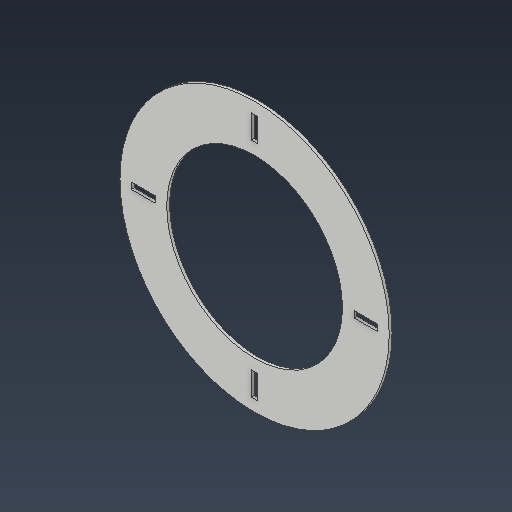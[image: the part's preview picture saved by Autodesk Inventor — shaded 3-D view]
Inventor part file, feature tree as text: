
AUTODESK INVENTOR PART (.ipt)
format: ipt  version: 2021 (Build 250183000, 183)  size: 138,752 bytes
history: native  units: mm
features: other x4, extrude x2, sketch x2, reference x2
ambient origin geometry x8: Origin, YZ Plane, XZ Plane, XY Plane, X Axis, Y Axis, Z Axis, Center Point
bodies: Body1 (feature_tree)
feature tree (10):
  extrude  "Выдавливание2"  Depth=1.5mm TaperAngle=0.0deg
  extrude  "Выдавливание3"  Depth=40.0mm TaperAngle=360.0deg
  sketch  "Эскиз3"
  reference  "Ссылка5"
  reference  "Ссылка6"
  sketch  "Эскиз4"
  other  "<userpath>\Documents\GitHub\Tesla_coil_V1\3dModels\TeslaCoil.iam"
  other  "TeslaCoil.iam"
  other  "Cap:2"
  other  "RackeSecondary:1"
